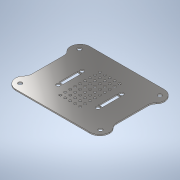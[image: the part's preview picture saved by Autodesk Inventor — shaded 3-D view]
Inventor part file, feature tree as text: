
AUTODESK INVENTOR PART (.ipt)
format: ipt  version: 2022 (Build 260153000, 153)  size: 256,000 bytes
history: native  units: in
note: dims shown in document units (in); Inventor stores cm internally (conversion verified against a paired STEP export)
features: sketch x6, extrude x3, hole x3
ambient origin geometry x8: Origin, YZ Plane, XZ Plane, XY Plane, X Axis, Y Axis, Z Axis, Center Point
bodies: Solid1 (feature_tree)
feature tree (12):
  extrude  "Extrusion1"  Depth=1.875in
  hole  "Hole1"  [1 undecoded]
  extrude  "Extrusion2"  Depth=0.752in
  hole  "Hole2"  [1 undecoded]
  extrude  "Extrusion3"  Depth=0.47in
  hole  "Hole3"  [1 undecoded]
  sketch  "Sketch1"  dims[d0=1.875in d1=2.375in]
  sketch  "Sketch2"  dims[d2=0.25in d3=0.0293in d4=0.0in]
  sketch  "Sketch3"  dims[d5=1.0157in d6=0.752in]
  sketch  "Sketch4"  dims[d7=0.752in d8=1.0157in]
  sketch  "Sketch5"  dims[d9=0.0984in d10=0.75in d11=0.119in d12=0.25in d13=0.5635in d14=1.0in d15=0.8108in d18=0.47in]
  sketch  "Sketch6"  dims[d19=0.0in d20=0.0in d21=0.1in d22=0.45in d23=0.45in d24=0.5in d25=0.25in d26=3.5433in d28=0.125in d29=1.9685in d31=0.125in d34=0.0625in d35=0.75in d36=0.375in d37=0.25in d38=0.5635in d39=1.0in d40=0.8108in d41=0.2in d42=45.0deg d43=0.2in d44=45.0deg d45=0.2in d46=45.0deg d47=0.2in d48=45.0deg d49=1.0in d50=0.0in d51=0.2in d52=45.0deg d53=0.2in d54=45.0deg d57=0.2in d58=45.0deg d59=0.2in d60=45.0deg d61=0.3in d62=0.3in d63=0.5in d64=0.5in d65=0.1in d66=0.094in d67=0.375in d68=0.25in d69=0.5635in d70=1.0in d71=0.8108in]
note: 3 required parameter values undecoded (feature->parameter linkage not recoverable at this tier; creation-order binding heuristic only, values carry confidence <= 0.55)
